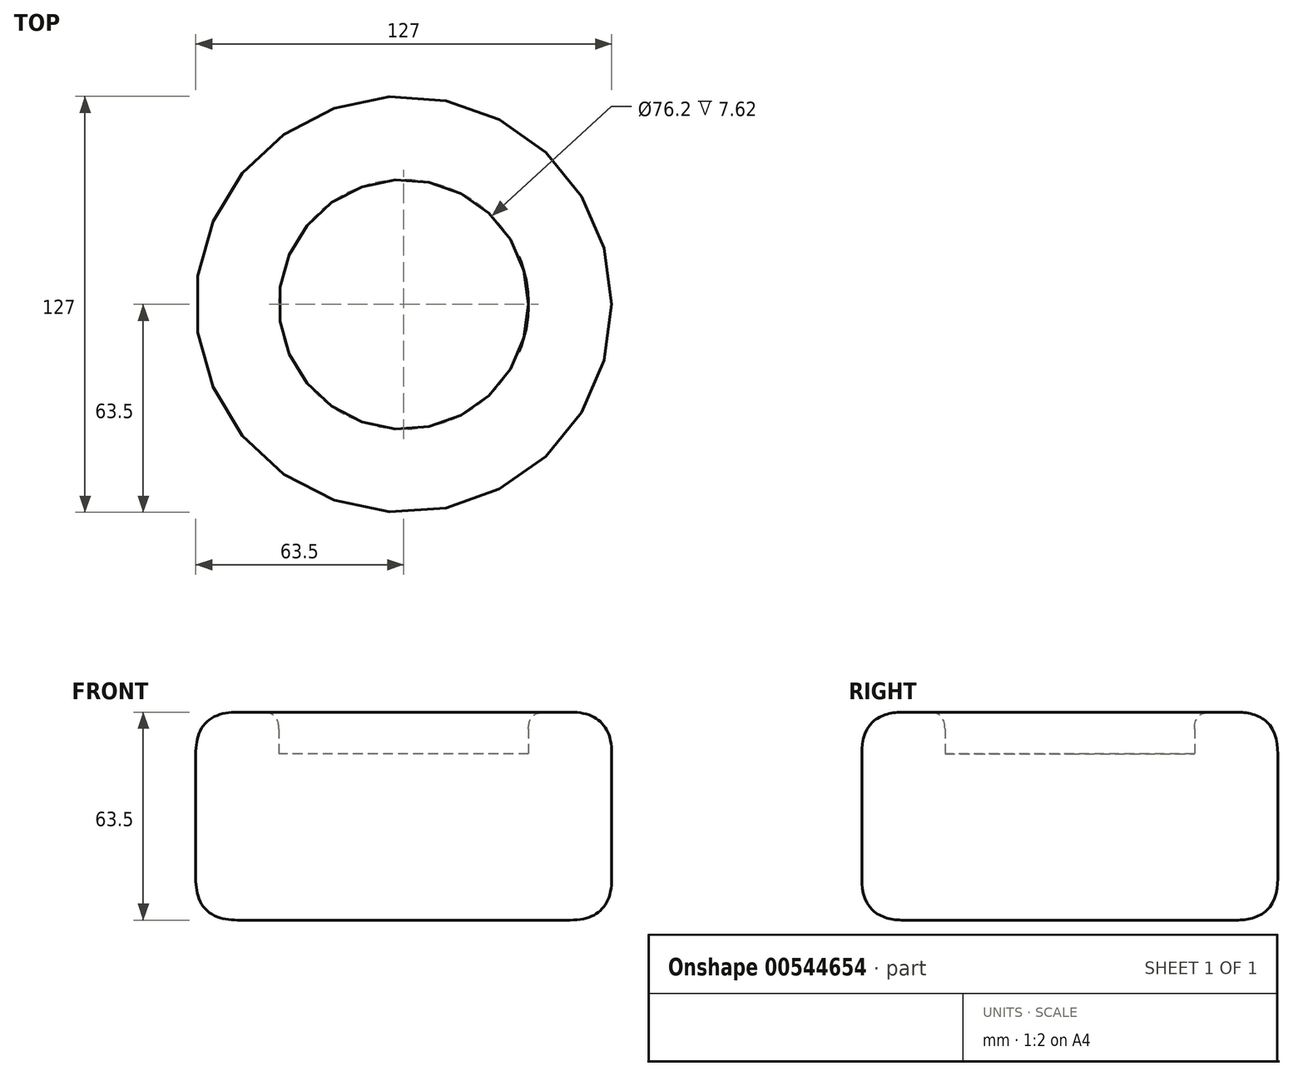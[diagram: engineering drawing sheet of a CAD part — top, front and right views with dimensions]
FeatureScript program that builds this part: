
annotation { "Feature Type Name" : "Feature", "Feature Type Description" : "" }
export const myFeature = defineFeature(function(context is Context, id is Id, definition is map)
    precondition{}
    {
        {
            var Q0;
            Q0=qCreatedBy(makeId("Top.planeOp"),FACE);
            var sketch = newSketch(context, id + "F0", { "sketchPlane" : qUnion([Q0])});
            skCircle(sketch, "E0", {"center": v(0, 0) * mm, "radius": 63.5 * mm});
            skCircle(sketch, "E1", {"center": v(0, 0) * mm, "radius": 38.1 * mm});
            skSolve(sketch);
        }
        {
            var Q0;
            Q0=makeQuery(id+"F0.imprint","IMPRINT",FACE,{"disambiguationData":[TD([[makeQuery(id+"F0.imprint","IMPRINT",EDGE,{"derivedFrom":sQuery(id+"F0.wireOp",EDGE,"E0")}),1.0]])]});
            extrude(context, id + "F1", {"entities" : qUnion([Q0]), "depth" : 63.5 * mm, "offsetDistance" : 25.4 * mm});
        }
        {
            var Q0;
            Q0=makeQuery(id+"F0.imprint","IMPRINT",FACE,{"disambiguationData":[TD([[makeQuery(id+"F0.imprint","IMPRINT",EDGE,{"derivedFrom":sQuery(id+"F0.wireOp",EDGE,"E1")}),1.0]])]});
            var Q1;
            Q1=sQuery(id+"F0.wireOp",EDGE,"E1");
            extrude(context, id + "F2", {"entities" : qUnion([Q0]), "operationType" : NewBodyOperationType.ADD, "surfaceEntities" : qUnion([Q1]), "depth" : 50.8 * mm, "offsetDistance" : 25.4 * mm});
        }
        {
            var Q0;
            Q0=makeQuery(id+"F1.opExtrude","CAP_EDGE",EDGE,{"disambiguationData":[OSD([sQuery(id+"F0.wireOp",EDGE,"E0")])],"isStart":false});
            fillet(context, id + "F3", {"entities" : qUnion([Q0]), "radius" : 12.7 * mm, "tangentPropagation" : true, "rho" : 0.5, "crossSection" : FilletCrossSection.CONIC, "allowEdgeOverflow" : false});
        }
        {
            var Q0;
            Q0=makeQuery(id+"F1.opExtrude","CAP_EDGE",EDGE,{"disambiguationData":[OSD([sQuery(id+"F0.wireOp",EDGE,"E0")])],"isStart":true});
            fillet(context, id + "F4", {"entities" : qUnion([Q0]), "radius" : 12.7 * mm, "tangentPropagation" : true, "rho" : 0.5, "crossSection" : FilletCrossSection.CONIC, "allowEdgeOverflow" : false});
        }
        {
            var Q0;
            Q0=makeQuery(id+"F1.opExtrude","CAP_EDGE",EDGE,{"disambiguationData":[OSD([sQuery(id+"F0.wireOp",EDGE,"E1")])],"isStart":false});
            fillet(context, id + "F5", {"entities" : qUnion([Q0]), "radius" : 5.08 * mm, "tangentPropagation" : true, "rho" : 0.5, "crossSection" : FilletCrossSection.CONIC, "allowEdgeOverflow" : false});
        }
    });
